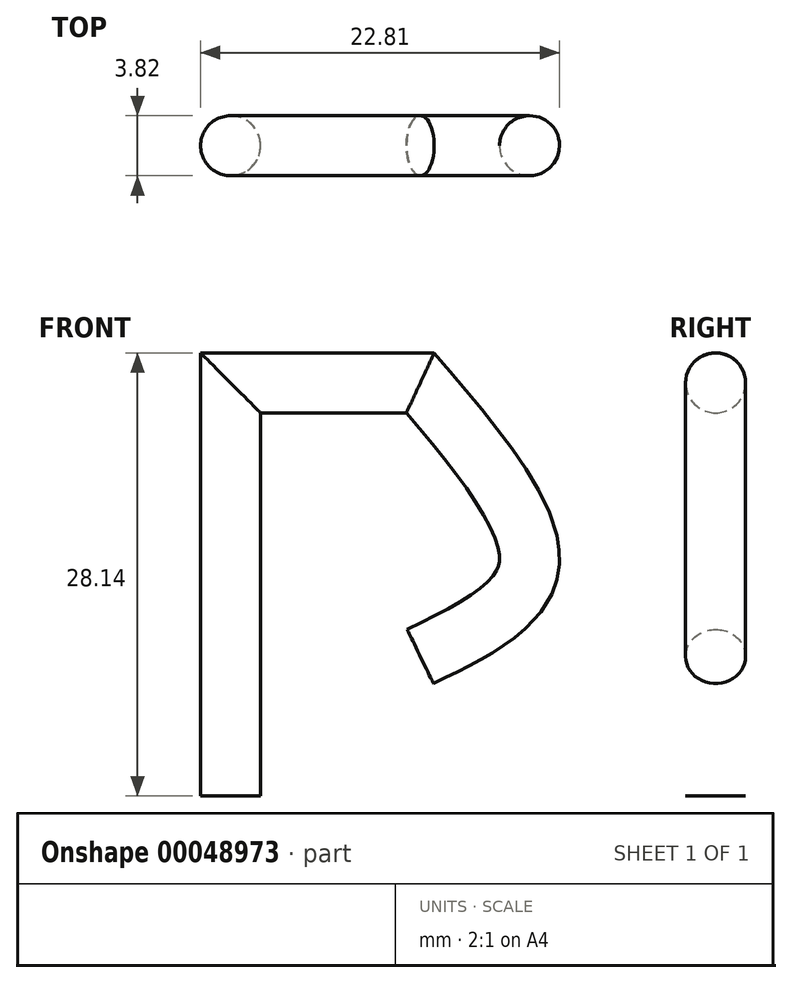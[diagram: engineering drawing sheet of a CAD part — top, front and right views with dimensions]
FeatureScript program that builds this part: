
annotation { "Feature Type Name" : "Feature", "Feature Type Description" : "" }
export const myFeature = defineFeature(function(context is Context, id is Id, definition is map)
    precondition{}
    {
        {
            var Q0;
            Q0=qCreatedBy(makeId("Top.planeOp"),FACE);
            var sketch = newSketch(context, id + "F0", { "sketchPlane" : qUnion([Q0])});
            skCircle(sketch, "E0", {"center": v(0, 0) * mm, "radius": 1.9 * mm});
            skSolve(sketch);
        }
        {
            var Q0;
            Q0=qCreatedBy(makeId("Front.planeOp"),FACE);
            var sketch = newSketch(context, id + "F1", { "sketchPlane" : qUnion([Q0])});
            skLineSegment(sketch, "E1", {"start": v(0, 0) * mm, "end": v(0, 26.23) * mm});
            skLineSegment(sketch, "E2", {"start": v(0, 26.23) * mm, "end": v(12.05, 26.23) * mm});
            skFitSpline(sketch, "E3", {"points": [v(12.05, 26.23) * mm, v(18.94, 14.43) * mm, v(12.05, 8.85) * mm], "startDerivative": vector(20.15, -23.75) * mm, "endDerivative": vector(-21.65, -10.53) * mm});
            skSolve(sketch);
        }
        {
            var Q0;
            Q0=makeQuery(id+"F0.imprint","IMPRINT",FACE,{"disambiguationData":[TD([[makeQuery(id+"F0.imprint","IMPRINT",EDGE,{"derivedFrom":sQuery(id+"F0.wireOp",EDGE,"E0")}),1.0]])]});
            var Q1;
            Q1=sQuery(id+"F1.wireOp",EDGE,"E1");
            var Q2;
            Q2=sQuery(id+"F1.wireOp",EDGE,"E2");
            var Q3;
            Q3=sQuery(id+"F1.wireOp",EDGE,"E3");
            sweep(context, id + "F2", {"profiles" : qUnion([Q0]), "path" : qUnion([Q1, Q2, Q3])});
        }
    });
